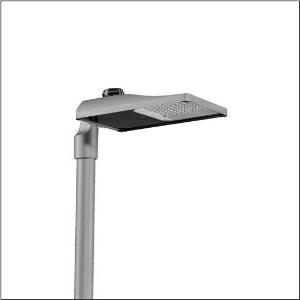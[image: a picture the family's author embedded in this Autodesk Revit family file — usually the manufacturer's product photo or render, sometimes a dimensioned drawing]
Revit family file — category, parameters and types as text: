
# Revit family: streetlight_sl_31_midi___pl52_5xh7h75n08ma_9a16
name_source: partatom
category: Lighting Fixtures
units: mm (PartAtom-declared; Revit-internal decimal feet)

## family parameters
Cut with Voids When Loaded = No
Host = Face
Light Source = No
Part Type = Normal
Room Calculation Point = No
Round Connector Dimension = Use Diameter
Shared = No

## types (1)
- --- (1 x LED, 15480 lm, 145.3 W, 2200K)
    Apparent Load = 145 VA
    CIE Flux Codes = 27 59 98 100 100
    Color Rendering = 70
    Color Temperature = 2200K
    Default Elevation = 1800 mm
    Description = Streetlight SL 31 midi NEMA (7pin), Desk-Remote mast luminaire for post-top, side-entry; light control with lens of PMMA; light distribution: PL52, direct asymmetric distribution, for standard-compliant lighting for roads and squares; LED: luminous flux: 15.480lm, light colour: 722, colour temperature: 2200K; luminous efficacy: 106,5lm/W; control: pre-setting: linear dimming characteristic, flexible luminous flux parameterisation, time-dependent luminous flux control, constant luminous flux control, intelligent temperature release in ECG and LED module, overheat protection; luminaire housing, of diecast aluminium, SITECO metallic grey (DB 702S), corrosivity category C5 high according to DIN EN ISO 12944; cover of toughened safety glass, transparent, opened without tools; mast flange of diecast aluminium, SITECO metallic grey (DB 702S), spigot size: 76/60mm, mast flange included unmounted; cable length: 12,5m, connection cable pre-assembled; mains connection: 220..240V, AC, 50/60Hz; power consumption (at start of service life): 145,3W / (at end of service life): 161,8W / (with reduced operation 50%): 61,1W; protection rating (complete): IP66; insulation class (complete): insulation class I (protective earthing); impact resistance: IK10; certification: CE, ENEC, ENEC+, VDE, UKCA; permissible operating ambient temperature for outdoor applications: -40..+50°C; packaging unit: 1 piece

Light Distribution: PL52
    Height = 79 mm
    Lamp = 1 x LED
    Lamp Light Flux = 15480 lm
    Lamp Power = 145.3 W
    Lamp count = 1
    Length = 577 mm
    Luminous efficacy = 107 lm/W
    Manufacturer = Siteco
    ModVariant = No
    Model = 5XH7H75N08MA
    Number of Poles = 1
    OnlyDefault = Yes
    Power Factor = 1
    Product Name = Streetlight SL 31 midi | PL52
    Product group = mast luminaire | pylon top
    ProductGroupID = 6100
    Protection Class = Protection class I
    Protection Degree = IP 66
    RLX_Detail_Level = 1
    RLX_Emergency_Light_Flux = 0 lm
    RLX_Emergency_Type = 0
    RLX_Emergency_Type_DB = No
    RlxData = <blob elided: 35849 chars, md5=e2ca6594>
    Socket = socket
    Standby Power = 0 W
    System Light Flux = 15480 lm
    System Power = 145 W
    Type Comments = factory setting: luminous flux: 100 % | dim-lin: 254 | 747 mA
    Type Image = l_1300282.jpg
    URL = http://relux.com
    VarID = @adj_009701
    Voltage = 0 V
    Weight = 0.00 kg
    Width = 362 mm

## geometry (parser evidence)
native form markers: Blend x4, Sweep x9
no freeform markers — native parametric forms only
